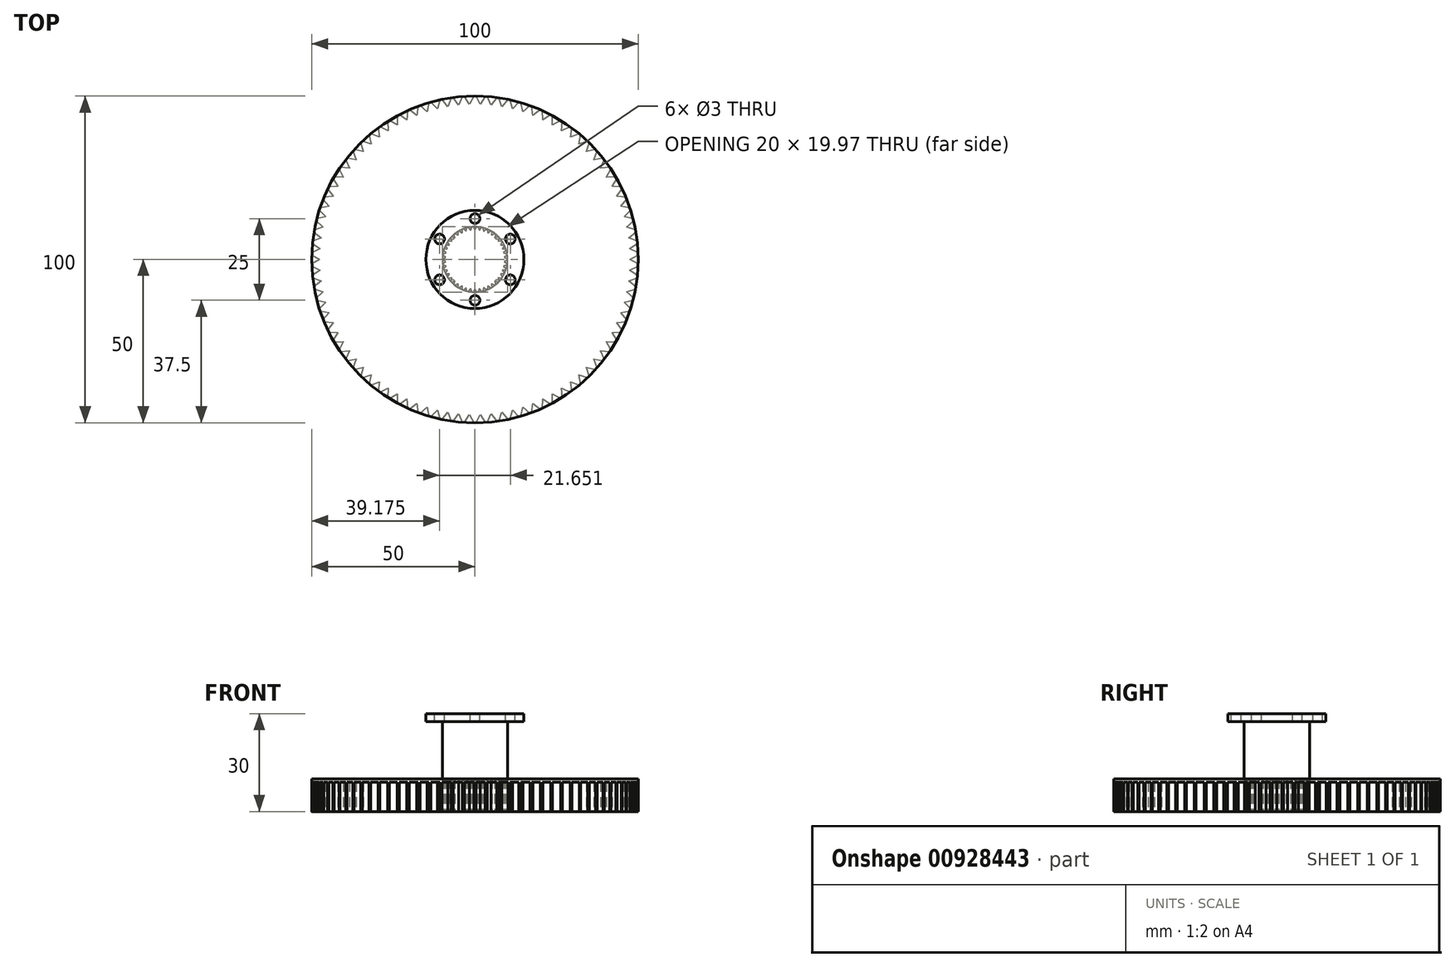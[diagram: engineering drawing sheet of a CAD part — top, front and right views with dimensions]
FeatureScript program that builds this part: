
annotation { "Feature Type Name" : "Feature", "Feature Type Description" : "" }
export const myFeature = defineFeature(function(context is Context, id is Id, definition is map)
    precondition{}
    {
        {
            var Q0;
            Q0=qCreatedBy(makeId("Top.planeOp"),FACE);
            var sketch = newSketch(context, id + "F0", { "sketchPlane" : qUnion([Q0])});
            skCircle(sketch, "E0", {"center": v(0, 0) * mm, "radius": 10 * mm});
            skSolve(sketch);
        }
        {
            var Q0;
            Q0 = qSketchRegion(id + "F0", true);
            extrude(context, id + "F1", {"entities" : qUnion([Q0]), "depth" : 15 * mm, "offsetDistance" : 25 * mm, "hasSecondDirection" : true, "secondDirectionOppositeDirection" : true, "secondDirectionDepth" : 12.5 * mm});
        }
        {
            var Q0;
            Q0=makeQuery(id+"F1.opExtrude","CAP_FACE",FACE,{"disambiguationData":[OSD([sQuery(id+"F0.wireOp",EDGE,"E0")])],"isStart":false});
            var sketch = newSketch(context, id + "F2", { "sketchPlane" : qUnion([Q0])});
            skCircle(sketch, "E1", {"center": v(0, 0) * mm, "radius": 15 * mm});
            skSolve(sketch);
        }
        {
            var Q0;
            Q0 = qSketchRegion(id + "F2", true);
            extrude(context, id + "F3", {"entities" : qUnion([Q0]), "operationType" : NewBodyOperationType.ADD, "depth" : 2.5 * mm, "offsetDistance" : 25 * mm});
        }
        {
            var Q0;
            Q0=makeQuery(id+"F3.opExtrude","CAP_FACE",FACE,{"disambiguationData":[OSD([sQuery(id+"F2.wireOp",EDGE,"E1")])],"isStart":false});
            var sketch = newSketch(context, id + "F4", { "sketchPlane" : qUnion([Q0])});
            skCircle(sketch, "E2", {"center": v(0, 0) * mm, "radius": 12.5 * mm, "construction": true});
            skLineSegment(sketch, "E3", {"start": v(0, 0) * mm, "end": v(0, 12.5) * mm, "construction": true});
            skCircle(sketch, "E4", {"center": v(0, 12.5) * mm, "radius": 1.5 * mm});
            skCircle(sketch, "E5.1.0", {"center": v(-10.83, 6.25) * mm, "radius": 1.5 * mm});
            skCircle(sketch, "E5.2.0", {"center": v(-10.83, -6.25) * mm, "radius": 1.5 * mm});
            skCircle(sketch, "E5.3.0", {"center": v(0, -12.5) * mm, "radius": 1.5 * mm});
            skCircle(sketch, "E5.4.0", {"center": v(10.83, -6.25) * mm, "radius": 1.5 * mm});
            skCircle(sketch, "E5.5.0", {"center": v(10.83, 6.25) * mm, "radius": 1.5 * mm});
            skLineSegment(sketch, "E5.anchor2", {"start": v(0, 0) * mm, "end": v(10.83, 6.25) * mm, "construction": true});
            skSolve(sketch);
        }
        {
            var Q0;
            Q0=makeQuery(id+"F4.imprint","IMPRINT",FACE,{"disambiguationData":[TD([[makeQuery(id+"F4.imprint","IMPRINT",EDGE,{"derivedFrom":sQuery(id+"F4.wireOp",EDGE,"E4")}),1.0]])]});
            var Q1;
            Q1=makeQuery(id+"F4.imprint","IMPRINT",FACE,{"disambiguationData":[TD([[makeQuery(id+"F4.imprint","IMPRINT",EDGE,{"derivedFrom":sQuery(id+"F4.wireOp",EDGE,"E5.5.0")}),1.0]])]});
            var Q2;
            Q2=makeQuery(id+"F4.imprint","IMPRINT",FACE,{"disambiguationData":[TD([[makeQuery(id+"F4.imprint","IMPRINT",EDGE,{"derivedFrom":sQuery(id+"F4.wireOp",EDGE,"E5.3.0")}),1.0]])]});
            var Q3;
            Q3=makeQuery(id+"F4.imprint","IMPRINT",FACE,{"disambiguationData":[TD([[makeQuery(id+"F4.imprint","IMPRINT",EDGE,{"derivedFrom":sQuery(id+"F4.wireOp",EDGE,"E5.1.0")}),1.0]])]});
            var Q4;
            Q4=makeQuery(id+"F4.imprint","IMPRINT",FACE,{"disambiguationData":[TD([[makeQuery(id+"F4.imprint","IMPRINT",EDGE,{"derivedFrom":sQuery(id+"F4.wireOp",EDGE,"E5.4.0")}),1.0]])]});
            var Q5;
            Q5=makeQuery(id+"F4.imprint","IMPRINT",FACE,{"disambiguationData":[TD([[makeQuery(id+"F4.imprint","IMPRINT",EDGE,{"derivedFrom":sQuery(id+"F4.wireOp",EDGE,"E5.2.0")}),1.0]])]});
            extrude(context, id + "F5", {"entities" : qUnion([Q0, Q1, Q2, Q3, Q4, Q5]), "operationType" : NewBodyOperationType.REMOVE, "oppositeDirection" : true, "depth" : 10 * mm, "offsetDistance" : 25 * mm});
        }
        {
            var Q0;
            Q0=makeQuery(id+"F1.opExtrude","CAP_FACE",FACE,{"disambiguationData":[OSD([sQuery(id+"F0.wireOp",EDGE,"E0")])],"isStart":true});
            var sketch = newSketch(context, id + "F6", { "sketchPlane" : qUnion([Q0])});
            skCircle(sketch, "E6", {"center": v(0, 0) * mm, "radius": 9.5 * mm, "construction": true});
            skLineSegment(sketch, "E7", {"start": v(0, 0) * mm, "end": v(0, 9.5) * mm, "construction": true});
            skPoint(sketch, "E8", {"position": v(0, 9) * mm});
            skLineSegment(sketch, "E9", {"start": v(0, 9) * mm, "end": v(-0.58, 10) * mm});
            skLineSegment(sketch, "E10", {"start": v(-0.58, 10) * mm, "end": v(0.58, 10) * mm});
            skLineSegment(sketch, "E11", {"start": v(0.58, 10) * mm, "end": v(0, 9) * mm});
            skLineSegment(sketch, "E12.1.0", {"start": v(-0.92, 9.97) * mm, "end": v(-1.34, 8.9) * mm});
            skLineSegment(sketch, "E12.1.1", {"start": v(-2.06, 9.8) * mm, "end": v(-0.92, 9.97) * mm});
            skLineSegment(sketch, "E12.1.2", {"start": v(-1.34, 8.9) * mm, "end": v(-2.06, 9.8) * mm});
            skLineSegment(sketch, "E12.2.0", {"start": v(-2.4, 9.73) * mm, "end": v(-2.65, 8.6) * mm});
            skLineSegment(sketch, "E12.2.1", {"start": v(-3.5, 9.39) * mm, "end": v(-2.4, 9.73) * mm});
            skLineSegment(sketch, "E12.2.2", {"start": v(-2.65, 8.6) * mm, "end": v(-3.5, 9.39) * mm});
            skLineSegment(sketch, "E12.3.0", {"start": v(-3.82, 9.26) * mm, "end": v(-3.9, 8.1) * mm});
            skLineSegment(sketch, "E12.3.1", {"start": v(-4.86, 8.76) * mm, "end": v(-3.82, 9.26) * mm});
            skLineSegment(sketch, "E12.3.2", {"start": v(-3.9, 8.1) * mm, "end": v(-4.86, 8.76) * mm});
            skLineSegment(sketch, "E12.4.0", {"start": v(-5.16, 8.59) * mm, "end": v(-5.07, 7.44) * mm});
            skLineSegment(sketch, "E12.4.1", {"start": v(-6.11, 7.94) * mm, "end": v(-5.16, 8.59) * mm});
            skLineSegment(sketch, "E12.4.2", {"start": v(-5.07, 7.44) * mm, "end": v(-6.11, 7.94) * mm});
            skLineSegment(sketch, "E12.5.0", {"start": v(-6.38, 7.72) * mm, "end": v(-6.12, 6.6) * mm});
            skLineSegment(sketch, "E12.5.1", {"start": v(-7.22, 6.94) * mm, "end": v(-6.38, 7.72) * mm});
            skLineSegment(sketch, "E12.5.2", {"start": v(-6.12, 6.6) * mm, "end": v(-7.22, 6.94) * mm});
            skLineSegment(sketch, "E12.6.0", {"start": v(-7.46, 6.69) * mm, "end": v(-7.04, 5.61) * mm});
            skLineSegment(sketch, "E12.6.1", {"start": v(-8.18, 5.78) * mm, "end": v(-7.46, 6.69) * mm});
            skLineSegment(sketch, "E12.6.2", {"start": v(-7.04, 5.61) * mm, "end": v(-8.18, 5.78) * mm});
            skLineSegment(sketch, "E12.7.0", {"start": v(-8.37, 5.5) * mm, "end": v(-7.8, 4.5) * mm});
            skLineSegment(sketch, "E12.7.1", {"start": v(-8.95, 4.5) * mm, "end": v(-8.37, 5.5) * mm});
            skLineSegment(sketch, "E12.7.2", {"start": v(-7.8, 4.5) * mm, "end": v(-8.95, 4.5) * mm});
            skLineSegment(sketch, "E12.8.0", {"start": v(-9.1, 4.2) * mm, "end": v(-8.38, 3.29) * mm});
            skLineSegment(sketch, "E12.8.1", {"start": v(-9.52, 3.12) * mm, "end": v(-9.1, 4.2) * mm});
            skLineSegment(sketch, "E12.8.2", {"start": v(-8.38, 3.29) * mm, "end": v(-9.52, 3.12) * mm});
            skLineSegment(sketch, "E12.9.0", {"start": v(-9.62, 2.79) * mm, "end": v(-8.77, 2) * mm});
            skLineSegment(sketch, "E12.9.1", {"start": v(-9.88, 1.66) * mm, "end": v(-9.62, 2.79) * mm});
            skLineSegment(sketch, "E12.9.2", {"start": v(-8.77, 2) * mm, "end": v(-9.88, 1.66) * mm});
            skLineSegment(sketch, "E12.10.0", {"start": v(-9.93, 1.32) * mm, "end": v(-8.97, 0.67) * mm});
            skLineSegment(sketch, "E12.10.1", {"start": v(-10.02, 0.17) * mm, "end": v(-9.93, 1.32) * mm});
            skLineSegment(sketch, "E12.10.2", {"start": v(-8.97, 0.67) * mm, "end": v(-10.02, 0.17) * mm});
            skLineSegment(sketch, "E12.11.0", {"start": v(-10.02, -0.17) * mm, "end": v(-8.97, -0.67) * mm});
            skLineSegment(sketch, "E12.11.1", {"start": v(-9.93, -1.32) * mm, "end": v(-10.02, -0.17) * mm});
            skLineSegment(sketch, "E12.11.2", {"start": v(-8.97, -0.67) * mm, "end": v(-9.93, -1.32) * mm});
            skLineSegment(sketch, "E12.12.0", {"start": v(-9.88, -1.66) * mm, "end": v(-8.77, -2) * mm});
            skLineSegment(sketch, "E12.12.1", {"start": v(-9.62, -2.79) * mm, "end": v(-9.88, -1.66) * mm});
            skLineSegment(sketch, "E12.12.2", {"start": v(-8.77, -2) * mm, "end": v(-9.62, -2.79) * mm});
            skLineSegment(sketch, "E12.13.0", {"start": v(-9.52, -3.12) * mm, "end": v(-8.38, -3.29) * mm});
            skLineSegment(sketch, "E12.13.1", {"start": v(-9.1, -4.2) * mm, "end": v(-9.52, -3.12) * mm});
            skLineSegment(sketch, "E12.13.2", {"start": v(-8.38, -3.29) * mm, "end": v(-9.1, -4.2) * mm});
            skLineSegment(sketch, "E12.14.0", {"start": v(-8.95, -4.5) * mm, "end": v(-7.8, -4.5) * mm});
            skLineSegment(sketch, "E12.14.1", {"start": v(-8.37, -5.5) * mm, "end": v(-8.95, -4.5) * mm});
            skLineSegment(sketch, "E12.14.2", {"start": v(-7.8, -4.5) * mm, "end": v(-8.37, -5.5) * mm});
            skLineSegment(sketch, "E12.15.0", {"start": v(-8.18, -5.78) * mm, "end": v(-7.04, -5.61) * mm});
            skLineSegment(sketch, "E12.15.1", {"start": v(-7.46, -6.69) * mm, "end": v(-8.18, -5.78) * mm});
            skLineSegment(sketch, "E12.15.2", {"start": v(-7.04, -5.61) * mm, "end": v(-7.46, -6.69) * mm});
            skLineSegment(sketch, "E12.16.0", {"start": v(-7.22, -6.94) * mm, "end": v(-6.12, -6.6) * mm});
            skLineSegment(sketch, "E12.16.1", {"start": v(-6.38, -7.72) * mm, "end": v(-7.22, -6.94) * mm});
            skLineSegment(sketch, "E12.16.2", {"start": v(-6.12, -6.6) * mm, "end": v(-6.38, -7.72) * mm});
            skLineSegment(sketch, "E12.17.0", {"start": v(-6.11, -7.94) * mm, "end": v(-5.07, -7.44) * mm});
            skLineSegment(sketch, "E12.17.1", {"start": v(-5.16, -8.59) * mm, "end": v(-6.11, -7.94) * mm});
            skLineSegment(sketch, "E12.17.2", {"start": v(-5.07, -7.44) * mm, "end": v(-5.16, -8.59) * mm});
            skLineSegment(sketch, "E12.18.0", {"start": v(-4.86, -8.76) * mm, "end": v(-3.9, -8.1) * mm});
            skLineSegment(sketch, "E12.18.1", {"start": v(-3.82, -9.26) * mm, "end": v(-4.86, -8.76) * mm});
            skLineSegment(sketch, "E12.18.2", {"start": v(-3.9, -8.1) * mm, "end": v(-3.82, -9.26) * mm});
            skLineSegment(sketch, "E12.19.0", {"start": v(-3.5, -9.39) * mm, "end": v(-2.65, -8.6) * mm});
            skLineSegment(sketch, "E12.19.1", {"start": v(-2.4, -9.73) * mm, "end": v(-3.5, -9.39) * mm});
            skLineSegment(sketch, "E12.19.2", {"start": v(-2.65, -8.6) * mm, "end": v(-2.4, -9.73) * mm});
            skLineSegment(sketch, "E12.20.0", {"start": v(-2.06, -9.8) * mm, "end": v(-1.34, -8.9) * mm});
            skLineSegment(sketch, "E12.20.1", {"start": v(-0.92, -9.97) * mm, "end": v(-2.06, -9.8) * mm});
            skLineSegment(sketch, "E12.20.2", {"start": v(-1.34, -8.9) * mm, "end": v(-0.92, -9.97) * mm});
            skLineSegment(sketch, "E12.21.0", {"start": v(-0.58, -10) * mm, "end": v(0, -9) * mm});
            skLineSegment(sketch, "E12.21.1", {"start": v(0.58, -10) * mm, "end": v(-0.58, -10) * mm});
            skLineSegment(sketch, "E12.21.2", {"start": v(0, -9) * mm, "end": v(0.58, -10) * mm});
            skLineSegment(sketch, "E12.22.0", {"start": v(0.92, -9.97) * mm, "end": v(1.34, -8.9) * mm});
            skLineSegment(sketch, "E12.22.1", {"start": v(2.06, -9.8) * mm, "end": v(0.92, -9.97) * mm});
            skLineSegment(sketch, "E12.22.2", {"start": v(1.34, -8.9) * mm, "end": v(2.06, -9.8) * mm});
            skLineSegment(sketch, "E12.23.0", {"start": v(2.4, -9.73) * mm, "end": v(2.65, -8.6) * mm});
            skLineSegment(sketch, "E12.23.1", {"start": v(3.5, -9.39) * mm, "end": v(2.4, -9.73) * mm});
            skLineSegment(sketch, "E12.23.2", {"start": v(2.65, -8.6) * mm, "end": v(3.5, -9.39) * mm});
            skLineSegment(sketch, "E12.24.0", {"start": v(3.82, -9.26) * mm, "end": v(3.9, -8.1) * mm});
            skLineSegment(sketch, "E12.24.1", {"start": v(4.86, -8.76) * mm, "end": v(3.82, -9.26) * mm});
            skLineSegment(sketch, "E12.24.2", {"start": v(3.9, -8.1) * mm, "end": v(4.86, -8.76) * mm});
            skLineSegment(sketch, "E12.25.0", {"start": v(5.16, -8.59) * mm, "end": v(5.07, -7.44) * mm});
            skLineSegment(sketch, "E12.25.1", {"start": v(6.11, -7.94) * mm, "end": v(5.16, -8.59) * mm});
            skLineSegment(sketch, "E12.25.2", {"start": v(5.07, -7.44) * mm, "end": v(6.11, -7.94) * mm});
            skLineSegment(sketch, "E12.26.0", {"start": v(6.38, -7.72) * mm, "end": v(6.12, -6.6) * mm});
            skLineSegment(sketch, "E12.26.1", {"start": v(7.22, -6.94) * mm, "end": v(6.38, -7.72) * mm});
            skLineSegment(sketch, "E12.26.2", {"start": v(6.12, -6.6) * mm, "end": v(7.22, -6.94) * mm});
            skLineSegment(sketch, "E12.27.0", {"start": v(7.46, -6.69) * mm, "end": v(7.04, -5.61) * mm});
            skLineSegment(sketch, "E12.27.1", {"start": v(8.18, -5.78) * mm, "end": v(7.46, -6.69) * mm});
            skLineSegment(sketch, "E12.27.2", {"start": v(7.04, -5.61) * mm, "end": v(8.18, -5.78) * mm});
            skLineSegment(sketch, "E12.28.0", {"start": v(8.37, -5.5) * mm, "end": v(7.8, -4.5) * mm});
            skLineSegment(sketch, "E12.28.1", {"start": v(8.95, -4.5) * mm, "end": v(8.37, -5.5) * mm});
            skLineSegment(sketch, "E12.28.2", {"start": v(7.8, -4.5) * mm, "end": v(8.95, -4.5) * mm});
            skLineSegment(sketch, "E12.29.0", {"start": v(9.1, -4.2) * mm, "end": v(8.38, -3.29) * mm});
            skLineSegment(sketch, "E12.29.1", {"start": v(9.52, -3.12) * mm, "end": v(9.1, -4.2) * mm});
            skLineSegment(sketch, "E12.29.2", {"start": v(8.38, -3.29) * mm, "end": v(9.52, -3.12) * mm});
            skLineSegment(sketch, "E12.30.0", {"start": v(9.62, -2.79) * mm, "end": v(8.77, -2) * mm});
            skLineSegment(sketch, "E12.30.1", {"start": v(9.88, -1.66) * mm, "end": v(9.62, -2.79) * mm});
            skLineSegment(sketch, "E12.30.2", {"start": v(8.77, -2) * mm, "end": v(9.88, -1.66) * mm});
            skLineSegment(sketch, "E12.31.0", {"start": v(9.93, -1.32) * mm, "end": v(8.97, -0.67) * mm});
            skLineSegment(sketch, "E12.31.1", {"start": v(10.02, -0.17) * mm, "end": v(9.93, -1.32) * mm});
            skLineSegment(sketch, "E12.31.2", {"start": v(8.97, -0.67) * mm, "end": v(10.02, -0.17) * mm});
            skLineSegment(sketch, "E12.32.0", {"start": v(10.02, 0.17) * mm, "end": v(8.97, 0.67) * mm});
            skLineSegment(sketch, "E12.32.1", {"start": v(9.93, 1.32) * mm, "end": v(10.02, 0.17) * mm});
            skLineSegment(sketch, "E12.32.2", {"start": v(8.97, 0.67) * mm, "end": v(9.93, 1.32) * mm});
            skLineSegment(sketch, "E12.33.0", {"start": v(9.88, 1.66) * mm, "end": v(8.77, 2) * mm});
            skLineSegment(sketch, "E12.33.1", {"start": v(9.62, 2.79) * mm, "end": v(9.88, 1.66) * mm});
            skLineSegment(sketch, "E12.33.2", {"start": v(8.77, 2) * mm, "end": v(9.62, 2.79) * mm});
            skLineSegment(sketch, "E12.34.0", {"start": v(9.52, 3.12) * mm, "end": v(8.38, 3.29) * mm});
            skLineSegment(sketch, "E12.34.1", {"start": v(9.1, 4.2) * mm, "end": v(9.52, 3.12) * mm});
            skLineSegment(sketch, "E12.34.2", {"start": v(8.38, 3.29) * mm, "end": v(9.1, 4.2) * mm});
            skLineSegment(sketch, "E12.35.0", {"start": v(8.95, 4.5) * mm, "end": v(7.8, 4.5) * mm});
            skLineSegment(sketch, "E12.35.1", {"start": v(8.37, 5.5) * mm, "end": v(8.95, 4.5) * mm});
            skLineSegment(sketch, "E12.35.2", {"start": v(7.8, 4.5) * mm, "end": v(8.37, 5.5) * mm});
            skLineSegment(sketch, "E12.36.0", {"start": v(8.18, 5.78) * mm, "end": v(7.04, 5.61) * mm});
            skLineSegment(sketch, "E12.36.1", {"start": v(7.46, 6.69) * mm, "end": v(8.18, 5.78) * mm});
            skLineSegment(sketch, "E12.36.2", {"start": v(7.04, 5.61) * mm, "end": v(7.46, 6.69) * mm});
            skLineSegment(sketch, "E12.37.0", {"start": v(7.22, 6.94) * mm, "end": v(6.12, 6.6) * mm});
            skLineSegment(sketch, "E12.37.1", {"start": v(6.38, 7.72) * mm, "end": v(7.22, 6.94) * mm});
            skLineSegment(sketch, "E12.37.2", {"start": v(6.12, 6.6) * mm, "end": v(6.38, 7.72) * mm});
            skLineSegment(sketch, "E12.38.0", {"start": v(6.11, 7.94) * mm, "end": v(5.07, 7.44) * mm});
            skLineSegment(sketch, "E12.38.1", {"start": v(5.16, 8.59) * mm, "end": v(6.11, 7.94) * mm});
            skLineSegment(sketch, "E12.38.2", {"start": v(5.07, 7.44) * mm, "end": v(5.16, 8.59) * mm});
            skLineSegment(sketch, "E12.39.0", {"start": v(4.86, 8.76) * mm, "end": v(3.9, 8.1) * mm});
            skLineSegment(sketch, "E12.39.1", {"start": v(3.82, 9.26) * mm, "end": v(4.86, 8.76) * mm});
            skLineSegment(sketch, "E12.39.2", {"start": v(3.9, 8.1) * mm, "end": v(3.82, 9.26) * mm});
            skLineSegment(sketch, "E12.40.0", {"start": v(3.5, 9.39) * mm, "end": v(2.65, 8.6) * mm});
            skLineSegment(sketch, "E12.40.1", {"start": v(2.4, 9.73) * mm, "end": v(3.5, 9.39) * mm});
            skLineSegment(sketch, "E12.40.2", {"start": v(2.65, 8.6) * mm, "end": v(2.4, 9.73) * mm});
            skLineSegment(sketch, "E12.41.0", {"start": v(2.06, 9.8) * mm, "end": v(1.34, 8.9) * mm});
            skLineSegment(sketch, "E12.41.1", {"start": v(0.92, 9.97) * mm, "end": v(2.06, 9.8) * mm});
            skLineSegment(sketch, "E12.41.2", {"start": v(1.34, 8.9) * mm, "end": v(0.92, 9.97) * mm});
            skSolve(sketch);
        }
        {
            var Q0;
            Q0 = qSketchRegion(id + "F6", true);
            extrude(context, id + "F7", {"entities" : qUnion([Q0]), "operationType" : NewBodyOperationType.REMOVE, "oppositeDirection" : true, "depth" : 10 * mm, "offsetDistance" : 25 * mm});
        }
        {
            var Q0;
            Q0=makeQuery(id+"F1.opExtrude","CAP_FACE",FACE,{"disambiguationData":[OSD([sQuery(id+"F0.wireOp",EDGE,"E0")])],"isStart":true});
            var sketch = newSketch(context, id + "F8", { "sketchPlane" : qUnion([Q0])});
            skCircle(sketch, "E13", {"center": v(0, 0) * mm, "radius": 50 * mm});
            skSolve(sketch);
        }
        {
            var Q0;
            Q0=makeQuery(id+"F8.imprint","IMPRINT",FACE,{"disambiguationData":[TD([[makeQuery(id+"F8.imprint","IMPRINT",EDGE,{"derivedFrom":sQuery(id+"F8.wireOp",EDGE,"E13")}),1.0]])]});
            extrude(context, id + "F9", {"entities" : qUnion([Q0]), "oppositeDirection" : true, "depth" : 10 * mm, "offsetDistance" : 25 * mm});
        }
        {
            var Q0;
            Q0=makeQuery(id+"F9.opExtrude","CAP_FACE",FACE,{"disambiguationData":[OSD([sQuery(id+"F0.wireOp",EDGE,"E0"),sQuery(id+"F6.wireOp",EDGE,"E9"),sQuery(id+"F6.wireOp",EDGE,"E11"),sQuery(id+"F6.wireOp",EDGE,"E12.1.0"),sQuery(id+"F6.wireOp",EDGE,"E12.1.2"),sQuery(id+"F6.wireOp",EDGE,"E12.2.0"),sQuery(id+"F6.wireOp",EDGE,"E12.2.2"),sQuery(id+"F6.wireOp",EDGE,"E12.3.0"),sQuery(id+"F6.wireOp",EDGE,"E12.3.2"),sQuery(id+"F6.wireOp",EDGE,"E12.4.0"),sQuery(id+"F6.wireOp",EDGE,"E12.4.2"),sQuery(id+"F6.wireOp",EDGE,"E12.5.0"),sQuery(id+"F6.wireOp",EDGE,"E12.5.2"),sQuery(id+"F6.wireOp",EDGE,"E12.6.0"),sQuery(id+"F6.wireOp",EDGE,"E12.6.2"),sQuery(id+"F6.wireOp",EDGE,"E12.7.0"),sQuery(id+"F6.wireOp",EDGE,"E12.7.2"),sQuery(id+"F6.wireOp",EDGE,"E12.8.0"),sQuery(id+"F6.wireOp",EDGE,"E12.8.2"),sQuery(id+"F6.wireOp",EDGE,"E12.9.0"),sQuery(id+"F6.wireOp",EDGE,"E12.9.2"),sQuery(id+"F6.wireOp",EDGE,"E12.10.0"),sQuery(id+"F6.wireOp",EDGE,"E12.10.2"),sQuery(id+"F6.wireOp",EDGE,"E12.11.0"),sQuery(id+"F6.wireOp",EDGE,"E12.11.2"),sQuery(id+"F6.wireOp",EDGE,"E12.12.0"),sQuery(id+"F6.wireOp",EDGE,"E12.12.2"),sQuery(id+"F6.wireOp",EDGE,"E12.13.0"),sQuery(id+"F6.wireOp",EDGE,"E12.13.2"),sQuery(id+"F6.wireOp",EDGE,"E12.14.0"),sQuery(id+"F6.wireOp",EDGE,"E12.14.2"),sQuery(id+"F6.wireOp",EDGE,"E12.15.0"),sQuery(id+"F6.wireOp",EDGE,"E12.15.2"),sQuery(id+"F6.wireOp",EDGE,"E12.16.0"),sQuery(id+"F6.wireOp",EDGE,"E12.16.2"),sQuery(id+"F6.wireOp",EDGE,"E12.17.0"),sQuery(id+"F6.wireOp",EDGE,"E12.17.2"),sQuery(id+"F6.wireOp",EDGE,"E12.18.0"),sQuery(id+"F6.wireOp",EDGE,"E12.18.2"),sQuery(id+"F6.wireOp",EDGE,"E12.19.0"),sQuery(id+"F6.wireOp",EDGE,"E12.19.2"),sQuery(id+"F6.wireOp",EDGE,"E12.20.0"),sQuery(id+"F6.wireOp",EDGE,"E12.20.2"),sQuery(id+"F6.wireOp",EDGE,"E12.21.0"),sQuery(id+"F6.wireOp",EDGE,"E12.21.2"),sQuery(id+"F6.wireOp",EDGE,"E12.22.0"),sQuery(id+"F6.wireOp",EDGE,"E12.22.2"),sQuery(id+"F6.wireOp",EDGE,"E12.23.0"),sQuery(id+"F6.wireOp",EDGE,"E12.23.2"),sQuery(id+"F6.wireOp",EDGE,"E12.24.0"),sQuery(id+"F6.wireOp",EDGE,"E12.24.2"),sQuery(id+"F6.wireOp",EDGE,"E12.25.0"),sQuery(id+"F6.wireOp",EDGE,"E12.25.2"),sQuery(id+"F6.wireOp",EDGE,"E12.26.0"),sQuery(id+"F6.wireOp",EDGE,"E12.26.2"),sQuery(id+"F6.wireOp",EDGE,"E12.27.0"),sQuery(id+"F6.wireOp",EDGE,"E12.27.2"),sQuery(id+"F6.wireOp",EDGE,"E12.28.0"),sQuery(id+"F6.wireOp",EDGE,"E12.28.2"),sQuery(id+"F6.wireOp",EDGE,"E12.29.0"),sQuery(id+"F6.wireOp",EDGE,"E12.29.2"),sQuery(id+"F6.wireOp",EDGE,"E12.30.0"),sQuery(id+"F6.wireOp",EDGE,"E12.30.2"),sQuery(id+"F6.wireOp",EDGE,"E12.31.0"),sQuery(id+"F6.wireOp",EDGE,"E12.31.2"),sQuery(id+"F6.wireOp",EDGE,"E12.32.0"),sQuery(id+"F6.wireOp",EDGE,"E12.32.2"),sQuery(id+"F6.wireOp",EDGE,"E12.33.0"),sQuery(id+"F6.wireOp",EDGE,"E12.33.2"),sQuery(id+"F6.wireOp",EDGE,"E12.34.0"),sQuery(id+"F6.wireOp",EDGE,"E12.34.2"),sQuery(id+"F6.wireOp",EDGE,"E12.35.0"),sQuery(id+"F6.wireOp",EDGE,"E12.35.2"),sQuery(id+"F6.wireOp",EDGE,"E12.36.0"),sQuery(id+"F6.wireOp",EDGE,"E12.36.2"),sQuery(id+"F6.wireOp",EDGE,"E12.37.0"),sQuery(id+"F6.wireOp",EDGE,"E12.37.2"),sQuery(id+"F6.wireOp",EDGE,"E12.38.0"),sQuery(id+"F6.wireOp",EDGE,"E12.38.2"),sQuery(id+"F6.wireOp",EDGE,"E12.39.0"),sQuery(id+"F6.wireOp",EDGE,"E12.39.2"),sQuery(id+"F6.wireOp",EDGE,"E12.40.0"),sQuery(id+"F6.wireOp",EDGE,"E12.40.2"),sQuery(id+"F6.wireOp",EDGE,"E12.41.0"),sQuery(id+"F6.wireOp",EDGE,"E12.41.2"),sQuery(id+"F8.wireOp",EDGE,"E13")])],"isStart":true});
            var sketch = newSketch(context, id + "F10", { "sketchPlane" : qUnion([Q0])});
            skCircle(sketch, "E14", {"center": v(0, 0) * mm, "radius": 47.5 * mm, "construction": true});
            skLineSegment(sketch, "E15", {"start": v(0, 0) * mm, "end": v(47.5, 0) * mm, "construction": true});
            skLineSegment(sketch, "E16", {"start": v(47.5, 0) * mm, "end": v(50.5, -1.73) * mm});
            skLineSegment(sketch, "E17", {"start": v(50.5, -1.73) * mm, "end": v(50.5, 1.73) * mm});
            skLineSegment(sketch, "E18", {"start": v(50.5, 1.73) * mm, "end": v(47.5, 0) * mm});
            skLineSegment(sketch, "E19.1.0", {"start": v(50.26, 5.25) * mm, "end": v(47.38, 3.31) * mm});
            skLineSegment(sketch, "E19.1.1", {"start": v(50.5, 1.8) * mm, "end": v(50.26, 5.25) * mm});
            skLineSegment(sketch, "E19.1.2", {"start": v(47.38, 3.31) * mm, "end": v(50.5, 1.8) * mm});
            skLineSegment(sketch, "E19.2.0", {"start": v(49.77, 8.74) * mm, "end": v(47.04, 6.61) * mm});
            skLineSegment(sketch, "E19.2.1", {"start": v(50.25, 5.31) * mm, "end": v(49.77, 8.74) * mm});
            skLineSegment(sketch, "E19.2.2", {"start": v(47.04, 6.61) * mm, "end": v(50.25, 5.31) * mm});
            skLineSegment(sketch, "E19.3.0", {"start": v(49.04, 12.2) * mm, "end": v(46.46, 9.88) * mm});
            skLineSegment(sketch, "E19.3.1", {"start": v(49.76, 8.8) * mm, "end": v(49.04, 12.2) * mm});
            skLineSegment(sketch, "E19.3.2", {"start": v(46.46, 9.88) * mm, "end": v(49.76, 8.8) * mm});
            skLineSegment(sketch, "E19.4.0", {"start": v(48.07, 15.58) * mm, "end": v(45.66, 13.1) * mm});
            skLineSegment(sketch, "E19.4.1", {"start": v(49.02, 12.25) * mm, "end": v(48.07, 15.58) * mm});
            skLineSegment(sketch, "E19.4.2", {"start": v(45.66, 13.1) * mm, "end": v(49.02, 12.25) * mm});
            skLineSegment(sketch, "E19.5.0", {"start": v(46.86, 18.9) * mm, "end": v(44.64, 16.25) * mm});
            skLineSegment(sketch, "E19.5.1", {"start": v(48.05, 15.64) * mm, "end": v(46.86, 18.9) * mm});
            skLineSegment(sketch, "E19.5.2", {"start": v(44.64, 16.25) * mm, "end": v(48.05, 15.64) * mm});
            skLineSegment(sketch, "E19.6.0", {"start": v(45.43, 22.12) * mm, "end": v(43.4, 19.32) * mm});
            skLineSegment(sketch, "E19.6.1", {"start": v(46.84, 18.96) * mm, "end": v(45.43, 22.12) * mm});
            skLineSegment(sketch, "E19.6.2", {"start": v(43.4, 19.32) * mm, "end": v(46.84, 18.96) * mm});
            skLineSegment(sketch, "E19.7.0", {"start": v(43.78, 25.24) * mm, "end": v(41.94, 22.3) * mm});
            skLineSegment(sketch, "E19.7.1", {"start": v(45.4, 22.18) * mm, "end": v(43.78, 25.24) * mm});
            skLineSegment(sketch, "E19.7.2", {"start": v(41.94, 22.3) * mm, "end": v(45.4, 22.18) * mm});
            skLineSegment(sketch, "E19.8.0", {"start": v(41.9, 28.23) * mm, "end": v(40.28, 25.17) * mm});
            skLineSegment(sketch, "E19.8.1", {"start": v(43.74, 25.3) * mm, "end": v(41.9, 28.23) * mm});
            skLineSegment(sketch, "E19.8.2", {"start": v(40.28, 25.17) * mm, "end": v(43.74, 25.3) * mm});
            skLineSegment(sketch, "E19.9.0", {"start": v(39.84, 31.08) * mm, "end": v(38.43, 27.92) * mm});
            skLineSegment(sketch, "E19.9.1", {"start": v(41.87, 28.28) * mm, "end": v(39.84, 31.08) * mm});
            skLineSegment(sketch, "E19.9.2", {"start": v(38.43, 27.92) * mm, "end": v(41.87, 28.28) * mm});
            skLineSegment(sketch, "E19.10.0", {"start": v(37.57, 33.79) * mm, "end": v(36.39, 30.53) * mm});
            skLineSegment(sketch, "E19.10.1", {"start": v(39.8, 31.13) * mm, "end": v(37.57, 33.79) * mm});
            skLineSegment(sketch, "E19.10.2", {"start": v(36.39, 30.53) * mm, "end": v(39.8, 31.13) * mm});
            skLineSegment(sketch, "E19.11.0", {"start": v(35.12, 36.33) * mm, "end": v(34.17, 33) * mm});
            skLineSegment(sketch, "E19.11.1", {"start": v(37.53, 33.83) * mm, "end": v(35.12, 36.33) * mm});
            skLineSegment(sketch, "E19.11.2", {"start": v(34.17, 33) * mm, "end": v(37.53, 33.83) * mm});
            skLineSegment(sketch, "E19.12.0", {"start": v(32.5, 38.69) * mm, "end": v(31.78, 35.3) * mm});
            skLineSegment(sketch, "E19.12.1", {"start": v(35.08, 36.37) * mm, "end": v(32.5, 38.69) * mm});
            skLineSegment(sketch, "E19.12.2", {"start": v(31.78, 35.3) * mm, "end": v(35.08, 36.37) * mm});
            skLineSegment(sketch, "E19.13.0", {"start": v(29.73, 40.86) * mm, "end": v(29.24, 37.43) * mm});
            skLineSegment(sketch, "E19.13.1", {"start": v(32.46, 38.73) * mm, "end": v(29.73, 40.86) * mm});
            skLineSegment(sketch, "E19.13.2", {"start": v(29.24, 37.43) * mm, "end": v(32.46, 38.73) * mm});
            skLineSegment(sketch, "E19.14.0", {"start": v(26.8, 42.83) * mm, "end": v(26.56, 39.38) * mm});
            skLineSegment(sketch, "E19.14.1", {"start": v(29.68, 40.9) * mm, "end": v(26.8, 42.83) * mm});
            skLineSegment(sketch, "E19.14.2", {"start": v(26.56, 39.38) * mm, "end": v(29.68, 40.9) * mm});
            skLineSegment(sketch, "E19.15.0", {"start": v(23.75, 44.6) * mm, "end": v(23.75, 41.14) * mm});
            skLineSegment(sketch, "E19.15.1", {"start": v(26.75, 42.87) * mm, "end": v(23.75, 44.6) * mm});
            skLineSegment(sketch, "E19.15.2", {"start": v(23.75, 41.14) * mm, "end": v(26.75, 42.87) * mm});
            skLineSegment(sketch, "E19.16.0", {"start": v(20.58, 46.15) * mm, "end": v(20.82, 42.7) * mm});
            skLineSegment(sketch, "E19.16.1", {"start": v(23.7, 44.63) * mm, "end": v(20.58, 46.15) * mm});
            skLineSegment(sketch, "E19.16.2", {"start": v(20.82, 42.7) * mm, "end": v(23.7, 44.63) * mm});
            skLineSegment(sketch, "E19.17.0", {"start": v(17.31, 47.47) * mm, "end": v(17.8, 44.04) * mm});
            skLineSegment(sketch, "E19.17.1", {"start": v(20.52, 46.17) * mm, "end": v(17.31, 47.47) * mm});
            skLineSegment(sketch, "E19.17.2", {"start": v(17.8, 44.04) * mm, "end": v(20.52, 46.17) * mm});
            skLineSegment(sketch, "E19.18.0", {"start": v(13.96, 48.56) * mm, "end": v(14.68, 45.18) * mm});
            skLineSegment(sketch, "E19.18.1", {"start": v(17.25, 47.5) * mm, "end": v(13.96, 48.56) * mm});
            skLineSegment(sketch, "E19.18.2", {"start": v(14.68, 45.18) * mm, "end": v(17.25, 47.5) * mm});
            skLineSegment(sketch, "E19.19.0", {"start": v(10.54, 49.42) * mm, "end": v(11.5, 46.09) * mm});
            skLineSegment(sketch, "E19.19.1", {"start": v(13.9, 48.58) * mm, "end": v(10.54, 49.42) * mm});
            skLineSegment(sketch, "E19.19.2", {"start": v(11.5, 46.09) * mm, "end": v(13.9, 48.58) * mm});
            skLineSegment(sketch, "E19.20.0", {"start": v(7.06, 50.03) * mm, "end": v(8.25, 46.78) * mm});
            skLineSegment(sketch, "E19.20.1", {"start": v(10.47, 49.43) * mm, "end": v(7.06, 50.03) * mm});
            skLineSegment(sketch, "E19.20.2", {"start": v(8.25, 46.78) * mm, "end": v(10.47, 49.43) * mm});
            skLineSegment(sketch, "E19.21.0", {"start": v(3.56, 50.4) * mm, "end": v(4.97, 47.24) * mm});
            skLineSegment(sketch, "E19.21.1", {"start": v(7, 50.04) * mm, "end": v(3.56, 50.4) * mm});
            skLineSegment(sketch, "E19.21.2", {"start": v(4.97, 47.24) * mm, "end": v(7, 50.04) * mm});
            skLineSegment(sketch, "E19.22.0", {"start": v(0.03, 50.53) * mm, "end": v(1.66, 47.47) * mm});
            skLineSegment(sketch, "E19.22.1", {"start": v(3.5, 50.4) * mm, "end": v(0.03, 50.53) * mm});
            skLineSegment(sketch, "E19.22.2", {"start": v(1.66, 47.47) * mm, "end": v(3.5, 50.4) * mm});
            skLineSegment(sketch, "E19.23.0", {"start": v(-3.5, 50.4) * mm, "end": v(-1.66, 47.47) * mm});
            skLineSegment(sketch, "E19.23.1", {"start": v(-0.03, 50.53) * mm, "end": v(-3.5, 50.4) * mm});
            skLineSegment(sketch, "E19.23.2", {"start": v(-1.66, 47.47) * mm, "end": v(-0.03, 50.53) * mm});
            skLineSegment(sketch, "E19.24.0", {"start": v(-7, 50.04) * mm, "end": v(-4.97, 47.24) * mm});
            skLineSegment(sketch, "E19.24.1", {"start": v(-3.56, 50.4) * mm, "end": v(-7, 50.04) * mm});
            skLineSegment(sketch, "E19.24.2", {"start": v(-4.97, 47.24) * mm, "end": v(-3.56, 50.4) * mm});
            skLineSegment(sketch, "E19.25.0", {"start": v(-10.47, 49.43) * mm, "end": v(-8.25, 46.78) * mm});
            skLineSegment(sketch, "E19.25.1", {"start": v(-7.06, 50.03) * mm, "end": v(-10.47, 49.43) * mm});
            skLineSegment(sketch, "E19.25.2", {"start": v(-8.25, 46.78) * mm, "end": v(-7.06, 50.03) * mm});
            skLineSegment(sketch, "E19.26.0", {"start": v(-13.9, 48.58) * mm, "end": v(-11.5, 46.09) * mm});
            skLineSegment(sketch, "E19.26.1", {"start": v(-10.54, 49.42) * mm, "end": v(-13.9, 48.58) * mm});
            skLineSegment(sketch, "E19.26.2", {"start": v(-11.5, 46.09) * mm, "end": v(-10.54, 49.42) * mm});
            skLineSegment(sketch, "E19.27.0", {"start": v(-17.25, 47.5) * mm, "end": v(-14.68, 45.18) * mm});
            skLineSegment(sketch, "E19.27.1", {"start": v(-13.96, 48.56) * mm, "end": v(-17.25, 47.5) * mm});
            skLineSegment(sketch, "E19.27.2", {"start": v(-14.68, 45.18) * mm, "end": v(-13.96, 48.56) * mm});
            skLineSegment(sketch, "E19.28.0", {"start": v(-20.52, 46.17) * mm, "end": v(-17.8, 44.04) * mm});
            skLineSegment(sketch, "E19.28.1", {"start": v(-17.31, 47.47) * mm, "end": v(-20.52, 46.17) * mm});
            skLineSegment(sketch, "E19.28.2", {"start": v(-17.8, 44.04) * mm, "end": v(-17.31, 47.47) * mm});
            skLineSegment(sketch, "E19.29.0", {"start": v(-23.7, 44.63) * mm, "end": v(-20.82, 42.7) * mm});
            skLineSegment(sketch, "E19.29.1", {"start": v(-20.58, 46.15) * mm, "end": v(-23.7, 44.63) * mm});
            skLineSegment(sketch, "E19.29.2", {"start": v(-20.82, 42.7) * mm, "end": v(-20.58, 46.15) * mm});
            skLineSegment(sketch, "E19.30.0", {"start": v(-26.75, 42.87) * mm, "end": v(-23.75, 41.14) * mm});
            skLineSegment(sketch, "E19.30.1", {"start": v(-23.75, 44.6) * mm, "end": v(-26.75, 42.87) * mm});
            skLineSegment(sketch, "E19.30.2", {"start": v(-23.75, 41.14) * mm, "end": v(-23.75, 44.6) * mm});
            skLineSegment(sketch, "E19.31.0", {"start": v(-29.68, 40.9) * mm, "end": v(-26.56, 39.38) * mm});
            skLineSegment(sketch, "E19.31.1", {"start": v(-26.8, 42.83) * mm, "end": v(-29.68, 40.9) * mm});
            skLineSegment(sketch, "E19.31.2", {"start": v(-26.56, 39.38) * mm, "end": v(-26.8, 42.83) * mm});
            skLineSegment(sketch, "E19.32.0", {"start": v(-32.46, 38.73) * mm, "end": v(-29.24, 37.43) * mm});
            skLineSegment(sketch, "E19.32.1", {"start": v(-29.73, 40.86) * mm, "end": v(-32.46, 38.73) * mm});
            skLineSegment(sketch, "E19.32.2", {"start": v(-29.24, 37.43) * mm, "end": v(-29.73, 40.86) * mm});
            skLineSegment(sketch, "E19.33.0", {"start": v(-35.08, 36.37) * mm, "end": v(-31.78, 35.3) * mm});
            skLineSegment(sketch, "E19.33.1", {"start": v(-32.5, 38.69) * mm, "end": v(-35.08, 36.37) * mm});
            skLineSegment(sketch, "E19.33.2", {"start": v(-31.78, 35.3) * mm, "end": v(-32.5, 38.69) * mm});
            skLineSegment(sketch, "E19.34.0", {"start": v(-37.53, 33.83) * mm, "end": v(-34.17, 33) * mm});
            skLineSegment(sketch, "E19.34.1", {"start": v(-35.12, 36.33) * mm, "end": v(-37.53, 33.83) * mm});
            skLineSegment(sketch, "E19.34.2", {"start": v(-34.17, 33) * mm, "end": v(-35.12, 36.33) * mm});
            skLineSegment(sketch, "E19.35.0", {"start": v(-39.8, 31.13) * mm, "end": v(-36.39, 30.53) * mm});
            skLineSegment(sketch, "E19.35.1", {"start": v(-37.57, 33.79) * mm, "end": v(-39.8, 31.13) * mm});
            skLineSegment(sketch, "E19.35.2", {"start": v(-36.39, 30.53) * mm, "end": v(-37.57, 33.79) * mm});
            skLineSegment(sketch, "E19.36.0", {"start": v(-41.87, 28.28) * mm, "end": v(-38.43, 27.92) * mm});
            skLineSegment(sketch, "E19.36.1", {"start": v(-39.84, 31.08) * mm, "end": v(-41.87, 28.28) * mm});
            skLineSegment(sketch, "E19.36.2", {"start": v(-38.43, 27.92) * mm, "end": v(-39.84, 31.08) * mm});
            skLineSegment(sketch, "E19.37.0", {"start": v(-43.74, 25.3) * mm, "end": v(-40.28, 25.17) * mm});
            skLineSegment(sketch, "E19.37.1", {"start": v(-41.9, 28.23) * mm, "end": v(-43.74, 25.3) * mm});
            skLineSegment(sketch, "E19.37.2", {"start": v(-40.28, 25.17) * mm, "end": v(-41.9, 28.23) * mm});
            skLineSegment(sketch, "E19.38.0", {"start": v(-45.4, 22.18) * mm, "end": v(-41.94, 22.3) * mm});
            skLineSegment(sketch, "E19.38.1", {"start": v(-43.78, 25.24) * mm, "end": v(-45.4, 22.18) * mm});
            skLineSegment(sketch, "E19.38.2", {"start": v(-41.94, 22.3) * mm, "end": v(-43.78, 25.24) * mm});
            skLineSegment(sketch, "E19.39.0", {"start": v(-46.84, 18.96) * mm, "end": v(-43.4, 19.32) * mm});
            skLineSegment(sketch, "E19.39.1", {"start": v(-45.43, 22.12) * mm, "end": v(-46.84, 18.96) * mm});
            skLineSegment(sketch, "E19.39.2", {"start": v(-43.4, 19.32) * mm, "end": v(-45.43, 22.12) * mm});
            skLineSegment(sketch, "E19.40.0", {"start": v(-48.05, 15.64) * mm, "end": v(-44.64, 16.25) * mm});
            skLineSegment(sketch, "E19.40.1", {"start": v(-46.86, 18.9) * mm, "end": v(-48.05, 15.64) * mm});
            skLineSegment(sketch, "E19.40.2", {"start": v(-44.64, 16.25) * mm, "end": v(-46.86, 18.9) * mm});
            skLineSegment(sketch, "E19.41.0", {"start": v(-49.02, 12.25) * mm, "end": v(-45.66, 13.1) * mm});
            skLineSegment(sketch, "E19.41.1", {"start": v(-48.07, 15.58) * mm, "end": v(-49.02, 12.25) * mm});
            skLineSegment(sketch, "E19.41.2", {"start": v(-45.66, 13.1) * mm, "end": v(-48.07, 15.58) * mm});
            skLineSegment(sketch, "E19.42.0", {"start": v(-49.76, 8.8) * mm, "end": v(-46.46, 9.88) * mm});
            skLineSegment(sketch, "E19.42.1", {"start": v(-49.04, 12.2) * mm, "end": v(-49.76, 8.8) * mm});
            skLineSegment(sketch, "E19.42.2", {"start": v(-46.46, 9.88) * mm, "end": v(-49.04, 12.2) * mm});
            skLineSegment(sketch, "E19.43.0", {"start": v(-50.25, 5.31) * mm, "end": v(-47.04, 6.61) * mm});
            skLineSegment(sketch, "E19.43.1", {"start": v(-49.77, 8.74) * mm, "end": v(-50.25, 5.31) * mm});
            skLineSegment(sketch, "E19.43.2", {"start": v(-47.04, 6.61) * mm, "end": v(-49.77, 8.74) * mm});
            skLineSegment(sketch, "E19.44.0", {"start": v(-50.5, 1.8) * mm, "end": v(-47.38, 3.31) * mm});
            skLineSegment(sketch, "E19.44.1", {"start": v(-50.26, 5.25) * mm, "end": v(-50.5, 1.8) * mm});
            skLineSegment(sketch, "E19.44.2", {"start": v(-47.38, 3.31) * mm, "end": v(-50.26, 5.25) * mm});
            skLineSegment(sketch, "E19.45.0", {"start": v(-50.5, -1.73) * mm, "end": v(-47.5, 0) * mm});
            skLineSegment(sketch, "E19.45.1", {"start": v(-50.5, 1.73) * mm, "end": v(-50.5, -1.73) * mm});
            skLineSegment(sketch, "E19.45.2", {"start": v(-47.5, 0) * mm, "end": v(-50.5, 1.73) * mm});
            skLineSegment(sketch, "E19.46.0", {"start": v(-50.26, -5.25) * mm, "end": v(-47.38, -3.31) * mm});
            skLineSegment(sketch, "E19.46.1", {"start": v(-50.5, -1.8) * mm, "end": v(-50.26, -5.25) * mm});
            skLineSegment(sketch, "E19.46.2", {"start": v(-47.38, -3.31) * mm, "end": v(-50.5, -1.8) * mm});
            skLineSegment(sketch, "E19.47.0", {"start": v(-49.77, -8.74) * mm, "end": v(-47.04, -6.61) * mm});
            skLineSegment(sketch, "E19.47.1", {"start": v(-50.25, -5.31) * mm, "end": v(-49.77, -8.74) * mm});
            skLineSegment(sketch, "E19.47.2", {"start": v(-47.04, -6.61) * mm, "end": v(-50.25, -5.31) * mm});
            skLineSegment(sketch, "E19.48.0", {"start": v(-49.04, -12.2) * mm, "end": v(-46.46, -9.88) * mm});
            skLineSegment(sketch, "E19.48.1", {"start": v(-49.76, -8.8) * mm, "end": v(-49.04, -12.2) * mm});
            skLineSegment(sketch, "E19.48.2", {"start": v(-46.46, -9.88) * mm, "end": v(-49.76, -8.8) * mm});
            skLineSegment(sketch, "E19.49.0", {"start": v(-48.07, -15.58) * mm, "end": v(-45.66, -13.1) * mm});
            skLineSegment(sketch, "E19.49.1", {"start": v(-49.02, -12.25) * mm, "end": v(-48.07, -15.58) * mm});
            skLineSegment(sketch, "E19.49.2", {"start": v(-45.66, -13.1) * mm, "end": v(-49.02, -12.25) * mm});
            skLineSegment(sketch, "E19.50.0", {"start": v(-46.86, -18.9) * mm, "end": v(-44.64, -16.25) * mm});
            skLineSegment(sketch, "E19.50.1", {"start": v(-48.05, -15.64) * mm, "end": v(-46.86, -18.9) * mm});
            skLineSegment(sketch, "E19.50.2", {"start": v(-44.64, -16.25) * mm, "end": v(-48.05, -15.64) * mm});
            skLineSegment(sketch, "E19.51.0", {"start": v(-45.43, -22.12) * mm, "end": v(-43.4, -19.32) * mm});
            skLineSegment(sketch, "E19.51.1", {"start": v(-46.84, -18.96) * mm, "end": v(-45.43, -22.12) * mm});
            skLineSegment(sketch, "E19.51.2", {"start": v(-43.4, -19.32) * mm, "end": v(-46.84, -18.96) * mm});
            skLineSegment(sketch, "E19.52.0", {"start": v(-43.78, -25.24) * mm, "end": v(-41.94, -22.3) * mm});
            skLineSegment(sketch, "E19.52.1", {"start": v(-45.4, -22.18) * mm, "end": v(-43.78, -25.24) * mm});
            skLineSegment(sketch, "E19.52.2", {"start": v(-41.94, -22.3) * mm, "end": v(-45.4, -22.18) * mm});
            skLineSegment(sketch, "E19.53.0", {"start": v(-41.9, -28.23) * mm, "end": v(-40.28, -25.17) * mm});
            skLineSegment(sketch, "E19.53.1", {"start": v(-43.74, -25.3) * mm, "end": v(-41.9, -28.23) * mm});
            skLineSegment(sketch, "E19.53.2", {"start": v(-40.28, -25.17) * mm, "end": v(-43.74, -25.3) * mm});
            skLineSegment(sketch, "E19.54.0", {"start": v(-39.84, -31.08) * mm, "end": v(-38.43, -27.92) * mm});
            skLineSegment(sketch, "E19.54.1", {"start": v(-41.87, -28.28) * mm, "end": v(-39.84, -31.08) * mm});
            skLineSegment(sketch, "E19.54.2", {"start": v(-38.43, -27.92) * mm, "end": v(-41.87, -28.28) * mm});
            skLineSegment(sketch, "E19.55.0", {"start": v(-37.57, -33.79) * mm, "end": v(-36.39, -30.53) * mm});
            skLineSegment(sketch, "E19.55.1", {"start": v(-39.8, -31.13) * mm, "end": v(-37.57, -33.79) * mm});
            skLineSegment(sketch, "E19.55.2", {"start": v(-36.39, -30.53) * mm, "end": v(-39.8, -31.13) * mm});
            skLineSegment(sketch, "E19.56.0", {"start": v(-35.12, -36.33) * mm, "end": v(-34.17, -33) * mm});
            skLineSegment(sketch, "E19.56.1", {"start": v(-37.53, -33.83) * mm, "end": v(-35.12, -36.33) * mm});
            skLineSegment(sketch, "E19.56.2", {"start": v(-34.17, -33) * mm, "end": v(-37.53, -33.83) * mm});
            skLineSegment(sketch, "E19.57.0", {"start": v(-32.5, -38.69) * mm, "end": v(-31.78, -35.3) * mm});
            skLineSegment(sketch, "E19.57.1", {"start": v(-35.08, -36.37) * mm, "end": v(-32.5, -38.69) * mm});
            skLineSegment(sketch, "E19.57.2", {"start": v(-31.78, -35.3) * mm, "end": v(-35.08, -36.37) * mm});
            skLineSegment(sketch, "E19.58.0", {"start": v(-29.73, -40.86) * mm, "end": v(-29.24, -37.43) * mm});
            skLineSegment(sketch, "E19.58.1", {"start": v(-32.46, -38.73) * mm, "end": v(-29.73, -40.86) * mm});
            skLineSegment(sketch, "E19.58.2", {"start": v(-29.24, -37.43) * mm, "end": v(-32.46, -38.73) * mm});
            skLineSegment(sketch, "E19.59.0", {"start": v(-26.8, -42.83) * mm, "end": v(-26.56, -39.38) * mm});
            skLineSegment(sketch, "E19.59.1", {"start": v(-29.68, -40.9) * mm, "end": v(-26.8, -42.83) * mm});
            skLineSegment(sketch, "E19.59.2", {"start": v(-26.56, -39.38) * mm, "end": v(-29.68, -40.9) * mm});
            skLineSegment(sketch, "E19.60.0", {"start": v(-23.75, -44.6) * mm, "end": v(-23.75, -41.14) * mm});
            skLineSegment(sketch, "E19.60.1", {"start": v(-26.75, -42.87) * mm, "end": v(-23.75, -44.6) * mm});
            skLineSegment(sketch, "E19.60.2", {"start": v(-23.75, -41.14) * mm, "end": v(-26.75, -42.87) * mm});
            skLineSegment(sketch, "E19.61.0", {"start": v(-20.58, -46.15) * mm, "end": v(-20.82, -42.7) * mm});
            skLineSegment(sketch, "E19.61.1", {"start": v(-23.7, -44.63) * mm, "end": v(-20.58, -46.15) * mm});
            skLineSegment(sketch, "E19.61.2", {"start": v(-20.82, -42.7) * mm, "end": v(-23.7, -44.63) * mm});
            skLineSegment(sketch, "E19.62.0", {"start": v(-17.31, -47.47) * mm, "end": v(-17.8, -44.04) * mm});
            skLineSegment(sketch, "E19.62.1", {"start": v(-20.52, -46.17) * mm, "end": v(-17.31, -47.47) * mm});
            skLineSegment(sketch, "E19.62.2", {"start": v(-17.8, -44.04) * mm, "end": v(-20.52, -46.17) * mm});
            skLineSegment(sketch, "E19.63.0", {"start": v(-13.96, -48.56) * mm, "end": v(-14.68, -45.18) * mm});
            skLineSegment(sketch, "E19.63.1", {"start": v(-17.25, -47.5) * mm, "end": v(-13.96, -48.56) * mm});
            skLineSegment(sketch, "E19.63.2", {"start": v(-14.68, -45.18) * mm, "end": v(-17.25, -47.5) * mm});
            skLineSegment(sketch, "E19.64.0", {"start": v(-10.54, -49.42) * mm, "end": v(-11.5, -46.09) * mm});
            skLineSegment(sketch, "E19.64.1", {"start": v(-13.9, -48.58) * mm, "end": v(-10.54, -49.42) * mm});
            skLineSegment(sketch, "E19.64.2", {"start": v(-11.5, -46.09) * mm, "end": v(-13.9, -48.58) * mm});
            skLineSegment(sketch, "E19.65.0", {"start": v(-7.06, -50.03) * mm, "end": v(-8.25, -46.78) * mm});
            skLineSegment(sketch, "E19.65.1", {"start": v(-10.47, -49.43) * mm, "end": v(-7.06, -50.03) * mm});
            skLineSegment(sketch, "E19.65.2", {"start": v(-8.25, -46.78) * mm, "end": v(-10.47, -49.43) * mm});
            skLineSegment(sketch, "E19.66.0", {"start": v(-3.56, -50.4) * mm, "end": v(-4.97, -47.24) * mm});
            skLineSegment(sketch, "E19.66.1", {"start": v(-7, -50.04) * mm, "end": v(-3.56, -50.4) * mm});
            skLineSegment(sketch, "E19.66.2", {"start": v(-4.97, -47.24) * mm, "end": v(-7, -50.04) * mm});
            skLineSegment(sketch, "E19.67.0", {"start": v(-0.03, -50.53) * mm, "end": v(-1.66, -47.47) * mm});
            skLineSegment(sketch, "E19.67.1", {"start": v(-3.5, -50.4) * mm, "end": v(-0.03, -50.53) * mm});
            skLineSegment(sketch, "E19.67.2", {"start": v(-1.66, -47.47) * mm, "end": v(-3.5, -50.4) * mm});
            skLineSegment(sketch, "E19.68.0", {"start": v(3.5, -50.4) * mm, "end": v(1.66, -47.47) * mm});
            skLineSegment(sketch, "E19.68.1", {"start": v(0.03, -50.53) * mm, "end": v(3.5, -50.4) * mm});
            skLineSegment(sketch, "E19.68.2", {"start": v(1.66, -47.47) * mm, "end": v(0.03, -50.53) * mm});
            skLineSegment(sketch, "E19.69.0", {"start": v(7, -50.04) * mm, "end": v(4.97, -47.24) * mm});
            skLineSegment(sketch, "E19.69.1", {"start": v(3.56, -50.4) * mm, "end": v(7, -50.04) * mm});
            skLineSegment(sketch, "E19.69.2", {"start": v(4.97, -47.24) * mm, "end": v(3.56, -50.4) * mm});
            skLineSegment(sketch, "E19.70.0", {"start": v(10.47, -49.43) * mm, "end": v(8.25, -46.78) * mm});
            skLineSegment(sketch, "E19.70.1", {"start": v(7.06, -50.03) * mm, "end": v(10.47, -49.43) * mm});
            skLineSegment(sketch, "E19.70.2", {"start": v(8.25, -46.78) * mm, "end": v(7.06, -50.03) * mm});
            skLineSegment(sketch, "E19.71.0", {"start": v(13.9, -48.58) * mm, "end": v(11.5, -46.09) * mm});
            skLineSegment(sketch, "E19.71.1", {"start": v(10.54, -49.42) * mm, "end": v(13.9, -48.58) * mm});
            skLineSegment(sketch, "E19.71.2", {"start": v(11.5, -46.09) * mm, "end": v(10.54, -49.42) * mm});
            skLineSegment(sketch, "E19.72.0", {"start": v(17.25, -47.5) * mm, "end": v(14.68, -45.18) * mm});
            skLineSegment(sketch, "E19.72.1", {"start": v(13.96, -48.56) * mm, "end": v(17.25, -47.5) * mm});
            skLineSegment(sketch, "E19.72.2", {"start": v(14.68, -45.18) * mm, "end": v(13.96, -48.56) * mm});
            skLineSegment(sketch, "E19.73.0", {"start": v(20.52, -46.17) * mm, "end": v(17.8, -44.04) * mm});
            skLineSegment(sketch, "E19.73.1", {"start": v(17.31, -47.47) * mm, "end": v(20.52, -46.17) * mm});
            skLineSegment(sketch, "E19.73.2", {"start": v(17.8, -44.04) * mm, "end": v(17.31, -47.47) * mm});
            skLineSegment(sketch, "E19.74.0", {"start": v(23.7, -44.63) * mm, "end": v(20.82, -42.7) * mm});
            skLineSegment(sketch, "E19.74.1", {"start": v(20.58, -46.15) * mm, "end": v(23.7, -44.63) * mm});
            skLineSegment(sketch, "E19.74.2", {"start": v(20.82, -42.7) * mm, "end": v(20.58, -46.15) * mm});
            skLineSegment(sketch, "E19.75.0", {"start": v(26.75, -42.87) * mm, "end": v(23.75, -41.14) * mm});
            skLineSegment(sketch, "E19.75.1", {"start": v(23.75, -44.6) * mm, "end": v(26.75, -42.87) * mm});
            skLineSegment(sketch, "E19.75.2", {"start": v(23.75, -41.14) * mm, "end": v(23.75, -44.6) * mm});
            skLineSegment(sketch, "E19.76.0", {"start": v(29.68, -40.9) * mm, "end": v(26.56, -39.38) * mm});
            skLineSegment(sketch, "E19.76.1", {"start": v(26.8, -42.83) * mm, "end": v(29.68, -40.9) * mm});
            skLineSegment(sketch, "E19.76.2", {"start": v(26.56, -39.38) * mm, "end": v(26.8, -42.83) * mm});
            skLineSegment(sketch, "E19.77.0", {"start": v(32.46, -38.73) * mm, "end": v(29.24, -37.43) * mm});
            skLineSegment(sketch, "E19.77.1", {"start": v(29.73, -40.86) * mm, "end": v(32.46, -38.73) * mm});
            skLineSegment(sketch, "E19.77.2", {"start": v(29.24, -37.43) * mm, "end": v(29.73, -40.86) * mm});
            skLineSegment(sketch, "E19.78.0", {"start": v(35.08, -36.37) * mm, "end": v(31.78, -35.3) * mm});
            skLineSegment(sketch, "E19.78.1", {"start": v(32.5, -38.69) * mm, "end": v(35.08, -36.37) * mm});
            skLineSegment(sketch, "E19.78.2", {"start": v(31.78, -35.3) * mm, "end": v(32.5, -38.69) * mm});
            skLineSegment(sketch, "E19.79.0", {"start": v(37.53, -33.83) * mm, "end": v(34.17, -33) * mm});
            skLineSegment(sketch, "E19.79.1", {"start": v(35.12, -36.33) * mm, "end": v(37.53, -33.83) * mm});
            skLineSegment(sketch, "E19.79.2", {"start": v(34.17, -33) * mm, "end": v(35.12, -36.33) * mm});
            skLineSegment(sketch, "E19.80.0", {"start": v(39.8, -31.13) * mm, "end": v(36.39, -30.53) * mm});
            skLineSegment(sketch, "E19.80.1", {"start": v(37.57, -33.79) * mm, "end": v(39.8, -31.13) * mm});
            skLineSegment(sketch, "E19.80.2", {"start": v(36.39, -30.53) * mm, "end": v(37.57, -33.79) * mm});
            skLineSegment(sketch, "E19.81.0", {"start": v(41.87, -28.28) * mm, "end": v(38.43, -27.92) * mm});
            skLineSegment(sketch, "E19.81.1", {"start": v(39.84, -31.08) * mm, "end": v(41.87, -28.28) * mm});
            skLineSegment(sketch, "E19.81.2", {"start": v(38.43, -27.92) * mm, "end": v(39.84, -31.08) * mm});
            skLineSegment(sketch, "E19.82.0", {"start": v(43.74, -25.3) * mm, "end": v(40.28, -25.17) * mm});
            skLineSegment(sketch, "E19.82.1", {"start": v(41.9, -28.23) * mm, "end": v(43.74, -25.3) * mm});
            skLineSegment(sketch, "E19.82.2", {"start": v(40.28, -25.17) * mm, "end": v(41.9, -28.23) * mm});
            skLineSegment(sketch, "E19.83.0", {"start": v(45.4, -22.18) * mm, "end": v(41.94, -22.3) * mm});
            skLineSegment(sketch, "E19.83.1", {"start": v(43.78, -25.24) * mm, "end": v(45.4, -22.18) * mm});
            skLineSegment(sketch, "E19.83.2", {"start": v(41.94, -22.3) * mm, "end": v(43.78, -25.24) * mm});
            skLineSegment(sketch, "E19.84.0", {"start": v(46.84, -18.96) * mm, "end": v(43.4, -19.32) * mm});
            skLineSegment(sketch, "E19.84.1", {"start": v(45.43, -22.12) * mm, "end": v(46.84, -18.96) * mm});
            skLineSegment(sketch, "E19.84.2", {"start": v(43.4, -19.32) * mm, "end": v(45.43, -22.12) * mm});
            skLineSegment(sketch, "E19.85.0", {"start": v(48.05, -15.64) * mm, "end": v(44.64, -16.25) * mm});
            skLineSegment(sketch, "E19.85.1", {"start": v(46.86, -18.9) * mm, "end": v(48.05, -15.64) * mm});
            skLineSegment(sketch, "E19.85.2", {"start": v(44.64, -16.25) * mm, "end": v(46.86, -18.9) * mm});
            skLineSegment(sketch, "E19.86.0", {"start": v(49.02, -12.25) * mm, "end": v(45.66, -13.1) * mm});
            skLineSegment(sketch, "E19.86.1", {"start": v(48.07, -15.58) * mm, "end": v(49.02, -12.25) * mm});
            skLineSegment(sketch, "E19.86.2", {"start": v(45.66, -13.1) * mm, "end": v(48.07, -15.58) * mm});
            skLineSegment(sketch, "E19.87.0", {"start": v(49.76, -8.8) * mm, "end": v(46.46, -9.88) * mm});
            skLineSegment(sketch, "E19.87.1", {"start": v(49.04, -12.2) * mm, "end": v(49.76, -8.8) * mm});
            skLineSegment(sketch, "E19.87.2", {"start": v(46.46, -9.88) * mm, "end": v(49.04, -12.2) * mm});
            skLineSegment(sketch, "E19.88.0", {"start": v(50.25, -5.31) * mm, "end": v(47.04, -6.61) * mm});
            skLineSegment(sketch, "E19.88.1", {"start": v(49.77, -8.74) * mm, "end": v(50.25, -5.31) * mm});
            skLineSegment(sketch, "E19.88.2", {"start": v(47.04, -6.61) * mm, "end": v(49.77, -8.74) * mm});
            skLineSegment(sketch, "E19.89.0", {"start": v(50.5, -1.8) * mm, "end": v(47.38, -3.31) * mm});
            skLineSegment(sketch, "E19.89.1", {"start": v(50.26, -5.25) * mm, "end": v(50.5, -1.8) * mm});
            skLineSegment(sketch, "E19.89.2", {"start": v(47.38, -3.31) * mm, "end": v(50.26, -5.25) * mm});
            skSolve(sketch);
        }
        {
            var Q0;
            Q0 = qSketchRegion(id + "F10", true);
            extrude(context, id + "F11", {"entities" : qUnion([Q0]), "operationType" : NewBodyOperationType.REMOVE, "oppositeDirection" : true, "depth" : 9 * mm, "offsetDistance" : 25 * mm});
        }
    });
